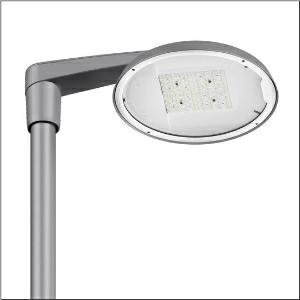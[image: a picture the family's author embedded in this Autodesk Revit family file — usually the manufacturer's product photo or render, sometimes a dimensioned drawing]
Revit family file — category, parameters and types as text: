
# Revit family: dl_r__50_iq_mini___st0_5a_5xa248b31f08le_a236
name_source: partatom
category: Lighting Fixtures
units: mm (PartAtom-declared; Revit-internal decimal feet)

## family parameters
Cut with Voids When Loaded = No
Host = Face
Light Source = No
Part Type = Normal
Room Calculation Point = No
Round Connector Dimension = Use Diameter
Shared = No

## types (1)
- --- (1 x LED, 10390 lm, 67.4 W, 3000K)
    Apparent Load = 67 VA
    CIE Flux Codes = 41 75 97 100 100
    Color Rendering = 70
    Color Temperature = 3000K
    Default Elevation = 1800 mm
    Description = DL® 50 iQ mini, mast luminaire, primary light control with lens, of PMMA, primary optical cover: cover, of toughened safety glass, transparent, light distribution: ST0.5a, light emission: direct distribution, primary light characteristic: asymmetric, installation type: side-entry, post-top, LED, High Power LED, rated luminous flux: 10.390lm, luminous efficacy: 154lm/W, light colour: 730, colour temperature: 3000K, control: optimised constant luminous flux control (CLO 2.0), Desk-Remote (wireless, voltage-free reading and setting of iQ features in the workshop via application-optimized NFC function/RFID function), Light-Fading, Smart-Wire, Night-Set, Lumen-Switch, Temp-Guard, Auto-Match, Street-Remote, mains connection: 230..240V, AC, 50/60Hz, connection cable pre-assembled, cable length: 8,5m, start of lifetime: 67W, end of service life: 70W, reduction: 31W, luminaire housing, of diecast aluminium, powder-coated, Siteco® metallic grey (DB 702S), inclination adjustable: 0°, 5°, 10° (post-top) | 0°, -5°, -10°, -15° (side-entry), please order mast post-top element or mast side-entry element separately, diameter: 500mm, height: 115mm, post-top: for spigot size d x l = 76 x 100mm; with reducer (optional accessory) 60 x 100mm | side-entry: for spigot size d x l = 60 x 100mm; with reducer (optional accessory) 42 x 100mm, protection rating (complete): IP66, insulation class (complete): insulation class II (safety insulation), certification: CE, ENEC, VDE, impact resistance: IK08, permissible operating ambient temperature for outdoor applications: -25..+40°C, standard-compliant lighting for roads and squares, packaging unit: 1 piece

Light Distribution: ST0.5a
    Height = 115 mm
    Lamp = 1 x LED
    Lamp Light Flux = 10390 lm
    Lamp Power = 67.4 W
    Lamp count = 1
    Length = 500 mm
    Luminous efficacy = 154 lm/W
    Manufacturer = Siteco
    ModVariant = No
    Model = 5XA248B31F08LE
    Number of Poles = 1
    OnlyDefault = Yes
    Power Factor = 1
    Product Name = DL® 50 iQ mini | ST0.5a
    Product group = mast luminaire | pylon top
    ProductGroupID = 6100
    Protection Class = Protection class II
    Protection Degree = IP 66
    RLX_Detail_Level = 1
    RLX_Emergency_Light_Flux = 0 lm
    RLX_Emergency_Type = 0
    RLX_Emergency_Type_DB = No
    RlxData = <blob elided: 127889 chars, md5=b13d9cb1>
    Socket = socket
    Standby Power = 0 W
    System Light Flux = 10390 lm
    System Power = 67 W
    Type Comments = factory setting: luminous flux: 100 % | dim-lin: 254 | 705 mA
    Type Image = l_1251790.jpg
    URL = http://relux.com
    VarID = @adj_092517
    Voltage = 0 V
    Weight = 0.00 kg
    Width = 0 mm  [stored 0 ft]

note: [stored X ft] marks values corroborated as IEEE doubles in the binary element streams (Revit-internal decimal feet)

## geometry (parser evidence)
native form markers: Blend x4, Sweep x11
no freeform markers — native parametric forms only
